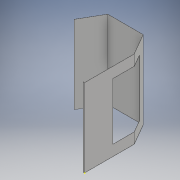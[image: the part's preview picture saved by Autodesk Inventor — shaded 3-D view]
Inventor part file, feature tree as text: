
AUTODESK INVENTOR PART (.ipt)
format: ipt  version: 2018 (Build 220112000, 112)  size: 133,120 bytes
history: native  units: mm
features: sketch x4, extrude x3
ambient origin geometry x8: Origin, YZ Plane, XZ Plane, XY Plane, X Axis, Y Axis, Z Axis, Center Point
bodies: Solid1 (feature_tree)
feature tree (7):
  extrude  "main"  Depth=700.0mm
  sketch  "Sketch2"  dims[d2=90.0deg d3=346.0mm]
  sketch  "Sketch3"  dims[d4=150.0deg d5=500.0mm]
  extrude  "Extrusion2"  Depth=346.0mm
  extrude  "Extrusion3"  Depth=500.0mm
  sketch  "Sketch1"  dims[d0=20.0mm d1=700.0mm]
  sketch  "Sketch4"  dims[d6=346.0mm d7=120.0deg d8=1.6mm d9=1100.0mm d10=0.0mm d13=800.0mm d14=300.0mm d16=800.0mm d17=200.0mm d18=1.6mm d19=0.0mm d20=1.6mm d21=0.0mm]
